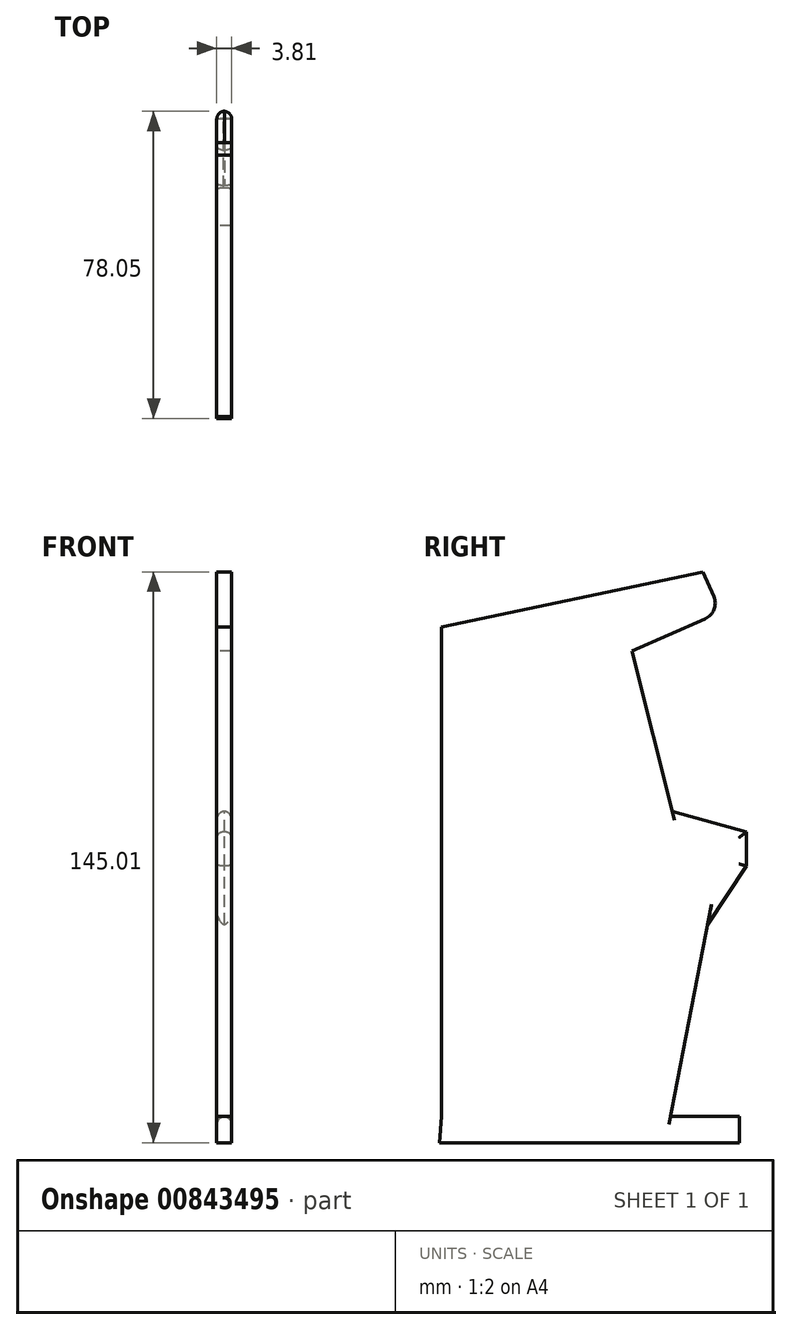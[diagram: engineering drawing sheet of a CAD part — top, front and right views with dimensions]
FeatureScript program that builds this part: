
annotation { "Feature Type Name" : "Feature", "Feature Type Description" : "" }
export const myFeature = defineFeature(function(context is Context, id is Id, definition is map)
    precondition{}
    {
        {
            var Q0;
            Q0=qCreatedBy(makeId("Right.planeOp"),FACE);
            var sketch = newSketch(context, id + "F0", { "sketchPlane" : qUnion([Q0])});
            skLineSegment(sketch, "E0", {"start": v(-48.49, 33.82) * mm, "end": v(-48.49, -63.62) * mm});
            skLineSegment(sketch, "E1", {"start": v(19.16, -14.9) * mm, "end": v(29.1, 0) * mm});
            skLineSegment(sketch, "E2", {"start": v(29.1, 0) * mm, "end": v(29.1, 8.75) * mm});
            skLineSegment(sketch, "E3", {"start": v(29.1, 8.75) * mm, "end": v(10.17, 13.95) * mm});
            skLineSegment(sketch, "E4", {"start": v(10.17, 13.95) * mm, "end": v(0, 54.64) * mm});
            skLineSegment(sketch, "E5", {"start": v(0, 54.64) * mm, "end": v(22.47, 64.57) * mm});
            skLineSegment(sketch, "E6", {"start": v(22.47, 64.57) * mm, "end": v(17.97, 74.76) * mm});
            skLineSegment(sketch, "E7", {"start": v(17.97, 74.76) * mm, "end": v(-48.49, 60.79) * mm});
            skLineSegment(sketch, "E8", {"start": v(-48.49, 60.79) * mm, "end": v(-48.49, 28.15) * mm});
            skLineSegment(sketch, "E9", {"start": v(-48.49, 28.15) * mm, "end": v(-48.49, -63.62) * mm});
            skLineSegment(sketch, "E10", {"start": v(19.16, -14.9) * mm, "end": v(9.7, -63.62) * mm});
            skLineSegment(sketch, "E11", {"start": v(9.7, -63.62) * mm, "end": v(27.2, -63.62) * mm});
            skLineSegment(sketch, "E12", {"start": v(27.2, -63.62) * mm, "end": v(27.2, -70.25) * mm});
            skLineSegment(sketch, "E13", {"start": v(27.2, -70.25) * mm, "end": v(-48.96, -70.25) * mm});
            skLineSegment(sketch, "E14", {"start": v(-48.96, -70.25) * mm, "end": v(-48.49, -63.62) * mm});
            skSolve(sketch);
        }
        {
            var Q0;
            Q0=makeQuery(id+"F0.imprint","IMPRINT",FACE,{"disambiguationData":[TD([[makeQuery(id+"F0.imprint","IMPRINT",EDGE,{"derivedFrom":sQuery(id+"F0.wireOp",EDGE,"E1")}),1.0]])]});
            extrude(context, id + "F1", {"entities" : qUnion([Q0]), "depth" : 3.8 * mm, "offsetDistance" : 25.4 * mm});
        }
        {
            var Q0;
            Q0=makeQuery(id+"F1.opExtrude","SWEPT_EDGE",EDGE,{"disambiguationData":[OSD([sQuery(id+"F0.wireOp",EDGE,"E5"),sQuery(id+"F0.wireOp",EDGE,"E6")])]});
            fillet(context, id + "F2", {"entities" : qUnion([Q0]), "radius" : 4.3 * mm, "tangentPropagation" : true, "allowEdgeOverflow" : false});
        }
        {
            var Q0;
            Q0=makeQuery(id+"F1.opExtrude","CAP_EDGE",EDGE,{"disambiguationData":[OSD([sQuery(id+"F0.wireOp",EDGE,"E11")])],"isStart":false});
            fillet(context, id + "F3", {"entities" : qUnion([Q0]), "radius" : 2.03 * mm, "tangentPropagation" : true, "allowEdgeOverflow" : false});
        }
        {
            var Q0;
            Q0=makeQuery(id+"F1.opExtrude","CAP_EDGE",EDGE,{"disambiguationData":[OSD([sQuery(id+"F0.wireOp",EDGE,"E11")])],"isStart":true});
            fillet(context, id + "F4", {"entities" : qUnion([Q0]), "radius" : 2.03 * mm, "tangentPropagation" : true, "allowEdgeOverflow" : false});
        }
        {
            var Q0;
            Q0=makeQuery(id+"F1.opExtrude","CAP_EDGE",EDGE,{"disambiguationData":[OSD([sQuery(id+"F0.wireOp",EDGE,"E1")])],"isStart":true});
            var Q1;
            Q1=makeQuery(id+"F1.opExtrude","CAP_EDGE",EDGE,{"disambiguationData":[OSD([sQuery(id+"F0.wireOp",EDGE,"E2")])],"isStart":true});
            var Q2;
            Q2=makeQuery(id+"F1.opExtrude","CAP_EDGE",EDGE,{"disambiguationData":[OSD([sQuery(id+"F0.wireOp",EDGE,"E3")])],"isStart":true});
            fillet(context, id + "F5", {"entities" : qUnion([Q0, Q1, Q2]), "radius" : 2.03 * mm, "tangentPropagation" : true, "allowEdgeOverflow" : false});
        }
        {
            var Q0;
            Q0=makeQuery(id+"F1.opExtrude","CAP_EDGE",EDGE,{"disambiguationData":[OSD([sQuery(id+"F0.wireOp",EDGE,"E3")])],"isStart":false});
            var Q1;
            Q1=makeQuery(id+"F1.opExtrude","CAP_EDGE",EDGE,{"disambiguationData":[OSD([sQuery(id+"F0.wireOp",EDGE,"E2")])],"isStart":false});
            var Q2;
            Q2=makeQuery(id+"F1.opExtrude","CAP_EDGE",EDGE,{"disambiguationData":[OSD([sQuery(id+"F0.wireOp",EDGE,"E1")])],"isStart":false});
            fillet(context, id + "F6", {"entities" : qUnion([Q0, Q1, Q2]), "radius" : 2.03 * mm, "tangentPropagation" : true, "allowEdgeOverflow" : false});
        }
    });
